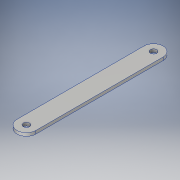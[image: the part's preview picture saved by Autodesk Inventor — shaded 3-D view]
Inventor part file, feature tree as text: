
AUTODESK INVENTOR PART (.ipt)
format: ipt  version: 2017 (Build 210142000, 142)  size: 102,400 bytes
history: native  units: in
note: dims shown in document units (in); Inventor stores cm internally (conversion verified against a paired STEP export)
features: extrude x1, sketch x1
ambient origin geometry x8: Origin, YZ Plane, XZ Plane, XY Plane, X Axis, Y Axis, Z Axis, Center Point
bodies: Solid1 (feature_tree)
feature tree (2):
  extrude  "Extrusion1"  Depth=0.75in
  sketch  "Sketch1"  dims[d0=5.0in d1=0.75in d2=0.25in d3=0.25in d4=0.125in d5=0.0in]
